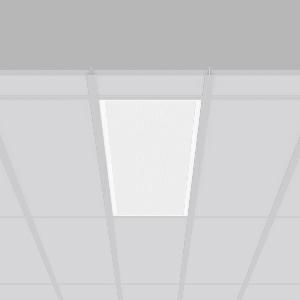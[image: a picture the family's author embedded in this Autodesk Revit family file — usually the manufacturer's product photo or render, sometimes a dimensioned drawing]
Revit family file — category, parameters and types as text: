
# Revit family: sidelite_eco_672367_002_1_3ef6
name_source: partatom
category: Lighting Fixtures
units: mm (PartAtom-declared; Revit-internal decimal feet)

## family parameters
Cut with Voids When Loaded = No
Host = Face
Light Source = No
Part Type = Normal
Room Calculation Point = No
Round Connector Dimension = Use Diameter
Shared = No

## types (1)
- SIDELITE ECO (1 x LED Modul 840, 3450 lm, 4000)
    Apparent Load = 29 VA
    CIE Flux Codes = 59 87 97 100 100
    Color Rendering = 80
    Color Temperature = 4000
    Default Elevation = 1800 mm
    Description = Series: SIDELITE ECO
Highly economical recessed luminaire with progressive LED technology. For escape route illumination. Frame made of aluminium, powder-coated. Diffuser plastic microprismatic. Lightguide and diffuser made of non-yellowing plastic (PMMA). Lateral light emission (RZB SIDELITE technology) for homogeneous light distribution. External driver. Second cable inlet for loop through. External driver with simple plug-in locking system. Extended connection cable (1.90 m). Suitable for connection to central battery systems. Luminaire can be used with accessories (to be ordered separately) for recessed, surface mounting or as pendant luminaire. 
Colour: white
Length: 1195 mm
Width: 295 mm
Cut-out length: 1170 mm
Cut-out width: 270 mm
Recess height: 160 mm
Luminaire: recess height: 40 mm
Weight: 3.39 kg
Operating mode: maintained power mode
Lamp: LED
Socket: without socket
Colour temperature: 4000K
Colour rendering index (CRI): 80
System power: 29 W
Rated luminous flux: 3450 lm
Luminous flux, emergency: 3450 lm
System power, emergency: 29 W
Control gear: Regulated power supply
Protection class: II
Type of protection: IP 20
    Height = 0 mm  [stored 0 ft]
    Lamp = 1 x LED Modul 840
    Lamp Light Flux = 3450 lm
    Lamp count = 1
    Length = 1195 mm
    Lifetime = 50000 h
    Luminous efficacy = 119 lm/W
    Manufacturer = RZB
    ModVariant = No
    Model = 672367.002.1
    Mounting Place = Ceiling
    Mounting Type = Recessed
    Number of Poles = 1
    OnlyDefault = Yes
    Power Factor = 1
    Product Name = SIDELITE ECO
    Product group = Recessed modular luminaires
    ProductGroupID = 406
    Protection Class = Protection class II
    Protection Degree = IP 20
    RLX_Detail_Level = 1
    RLX_Emergency_Light_Flux = 3450 lm
    RLX_Emergency_Type = 3
    RLX_Emergency_Type_DB = Yes
    RlxData = <blob elided: 34793 chars, md5=e07035c1>
    Socket = socket
    Standby Power = 0 W
    System Light Flux = 3450 lm
    System Power = 29 W
    Type Comments = Product without accessories
    Type Image = 312366.002.jpg
    URL = http://relux.com
    VarID = ---
    Voltage = 230 V
    Voltage Range = 220-240 V
    Weight = 0.00 kg
    Width = 295 mm

note: [stored X ft] marks values corroborated as IEEE doubles in the binary element streams (Revit-internal decimal feet)

## geometry (parser evidence)
native form markers: Blend x4, Sweep x10
no freeform markers — native parametric forms only
